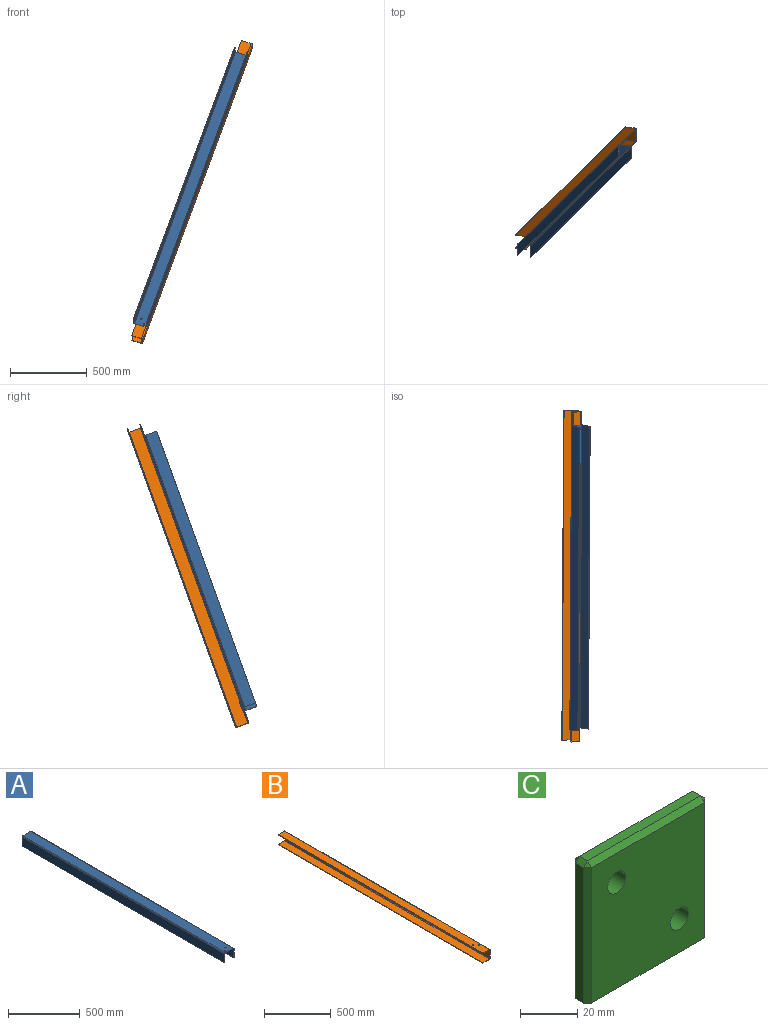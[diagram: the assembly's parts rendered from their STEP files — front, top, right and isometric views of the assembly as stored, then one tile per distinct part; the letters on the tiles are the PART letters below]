
ASSEMBLY  parts=3 mates=1
PART A: 18 faces, bbox 92.5x1996x84 mm
  f0: plane 1996x76.5mm, normal (0,0,1), area 152513.1mm2, adj f1,f9,f12,f13,f14,f15,f16,f17
  f1: cylinder r=8mm len=1992mm, axis (0,-1,0), area 25032.2mm2, adj f0,f10,f12,f14
  f2: plane 1992x4mm, normal (0,0,-1), area 7968mm2, adj f3,f10,f12,f14
  f3: plane 1992x76mm, normal (1,0,0), area 151392mm2, adj f2,f4,f12,f14
  f4: cylinder r=4mm len=1992mm, axis (0,-1,0), area 12516.1mm2, adj f3,f5,f12,f14
  f5: plane 1996x76.5mm, normal (0,0,-1), area 152513.1mm2, adj f4,f11,f12,f13,f14,f15,f16,f17
  f6: plane 1996x76mm, normal (-1,0,0), area 151696mm2, adj f7,f11,f12,f13
  f7: plane 1996x4mm, normal (0,0,-1), area 7984mm2, adj f6,f8,f12,f13
  f8: plane 1996x76mm, normal (1,0,0), area 151696mm2, adj f7,f9,f12,f13
  f9: cylinder r=8mm len=1996mm, axis (0,-1,0), area 25082.5mm2, adj f0,f8,f12,f13
  f10: plane 1992x76mm, normal (-1,0,0), area 151392mm2, adj f1,f2,f12,f14
  f11: cylinder r=4mm len=1996mm, axis (0,-1,0), area 12541.2mm2, adj f5,f6,f12,f13
  f12: plane 92.5x84mm, normal (0,1,0), area 989.4mm2, adj f0,f1,f2,f3,f4,f5,f6,f7
  f13: plane 84x71.09mm, normal (0,-1,0), area 594.1mm2, adj f0,f5,f6,f7,f8,f9,f11,f15
  f14: plane 84x21.41mm, normal (0,-1,0), area 395.3mm2, adj f0,f1,f2,f3,f4,f5,f10,f15
  f15: plane 4x4mm, normal (-1,0,0), area 16mm2, adj f0,f5,f13,f14
  f16: cylinder r=4.5mm len=9mm, axis (0,0,-1), area 113.1mm2, adj f0,f5
  f17: cylinder r=4.5mm len=9mm, axis (0,0,-1), area 113.1mm2, adj f0,f5
PART B: 16 faces, bbox 75x2168x92.5 mm
  f0: plane 2168x4mm, normal (-1,0,0), area 8672mm2, adj f1,f11,f12,f13
  f1: plane 2168x67mm, normal (0,0,-1), area 145128.8mm2, adj f0,f2,f12,f13,f14,f15
  f2: cylinder r=4mm len=2168mm, axis (0,-1,0), area 13621.9mm2, adj f1,f3,f12,f13
  f3: plane 2168x76.5mm, normal (-1,0,0), area 165852mm2, adj f2,f4,f12,f13
  f4: cylinder r=4mm len=2168mm, axis (0,-1,0), area 13621.9mm2, adj f3,f5,f12,f13
  f5: plane 2168x67mm, normal (0,0,1), area 145256mm2, adj f4,f6,f12,f13
  f6: plane 2168x4mm, normal (-1,0,0), area 8672mm2, adj f5,f7,f12,f13
  f7: plane 2168x67mm, normal (0,0,-1), area 145256mm2, adj f6,f8,f12,f13
  f8: cylinder r=8mm len=2168mm, axis (0,-1,0), area 27243.9mm2, adj f7,f9,f12,f13
  f9: plane 2168x76.5mm, normal (1,0,0), area 165852mm2, adj f8,f10,f12,f13
  f10: cylinder r=8mm len=2168mm, axis (0,-1,0), area 27243.9mm2, adj f9,f11,f12,f13
  f11: plane 2168x67mm, normal (0,0,1), area 145128.8mm2, adj f0,f10,f12,f13,f14,f15
  f12: plane 92.5x75mm, normal (0,1,0), area 917.4mm2, adj f0,f1,f2,f3,f4,f5,f6,f7
  f13: plane 92.5x75mm, normal (0,-1,0), area 917.4mm2, adj f0,f1,f2,f3,f4,f5,f6,f7
  f14: cylinder r=4.5mm len=9mm, axis (0,0,1), area 113.1mm2, adj f1,f11
  f15: cylinder r=4.5mm len=9mm, axis (0,0,1), area 113.1mm2, adj f1,f11
PART C: 20 faces, bbox 60x8x60 mm
  f0: plane 56x4mm, normal (0,0,1), area 224mm2, adj f11,f12,f16,f17
  f1: plane 58x4mm, normal (-1,0,0), area 232mm2, adj f2,f13,f17,f19
  f2: plane 60x8mm, normal (0,0,-1), area 472mm2, adj f1,f5,f6,f7,f8,f10,f13,f19
  f3: cylinder r=4.5mm len=9mm, axis (0,1,0), area 226.2mm2, adj f6,f7
  f4: cylinder r=4.5mm len=9mm, axis (0,1,0), area 226.2mm2, adj f6,f7
  f5: plane 58x4mm, normal (1,0,0), area 232mm2, adj f2,f8,f10,f11
  f6: plane 58x56mm, normal (0,-1,0), area 3120.8mm2, adj f2,f3,f4,f8,f12,f13
  f7: plane 58x56mm, normal (0,1,0), area 3120.8mm2, adj f2,f3,f4,f10,f16,f19
  f8: plane 58x2mm, normal (0.71,-0.71,0), area 164mm2, adj f2,f5,f6,f9
  f9: plane 2x2mm, normal (0.58,-0.58,0.58), area 3.5mm2, adj f8,f11,f12
  f10: plane 58x2mm, normal (0.71,0.71,0), area 164mm2, adj f2,f5,f7,f14
  f11: plane 4x2mm, normal (0.71,0,0.71), area 11.3mm2, adj f0,f5,f9,f14
  f12: plane 56x2mm, normal (0,-0.71,0.71), area 158.4mm2, adj f0,f6,f9,f15
  f13: plane 58x2mm, normal (-0.71,-0.71,0), area 164mm2, adj f1,f2,f6,f15
  f14: plane 2x2mm, normal (0.58,0.58,0.58), area 3.5mm2, adj f10,f11,f16
  f15: plane 2x2mm, normal (-0.58,-0.58,0.58), area 3.5mm2, adj f12,f13,f17
  f16: plane 56x2mm, normal (0,0.71,0.71), area 158.4mm2, adj f0,f7,f14,f18
  f17: plane 4x2mm, normal (-0.71,0,0.71), area 11.3mm2, adj f0,f1,f15,f18
  f18: plane 2x2mm, normal (-0.58,0.58,0.58), area 3.5mm2, adj f16,f17,f19
  f19: plane 58x2mm, normal (-0.71,0.71,0), area 164mm2, adj f1,f2,f7,f18
PLACE A rot(axis=(-0.14,-0.81,-0.57),169deg) t=(-69.24,-22.13,-140.93)mm
PLACE B rot(axis=(0.96,0.16,-0.23),72.3deg) t=(-88.54,32.89,-247.87)mm
PLACE C rot(axis=(-0.71,0.69,-0.12),27.7deg) t=(-51.07,33.55,-134.11)mm
MATE fastened B.f14 <-> A.f17  axis (0,-0.94,0.34) through (-41.56,19.28,-149.93)mm
